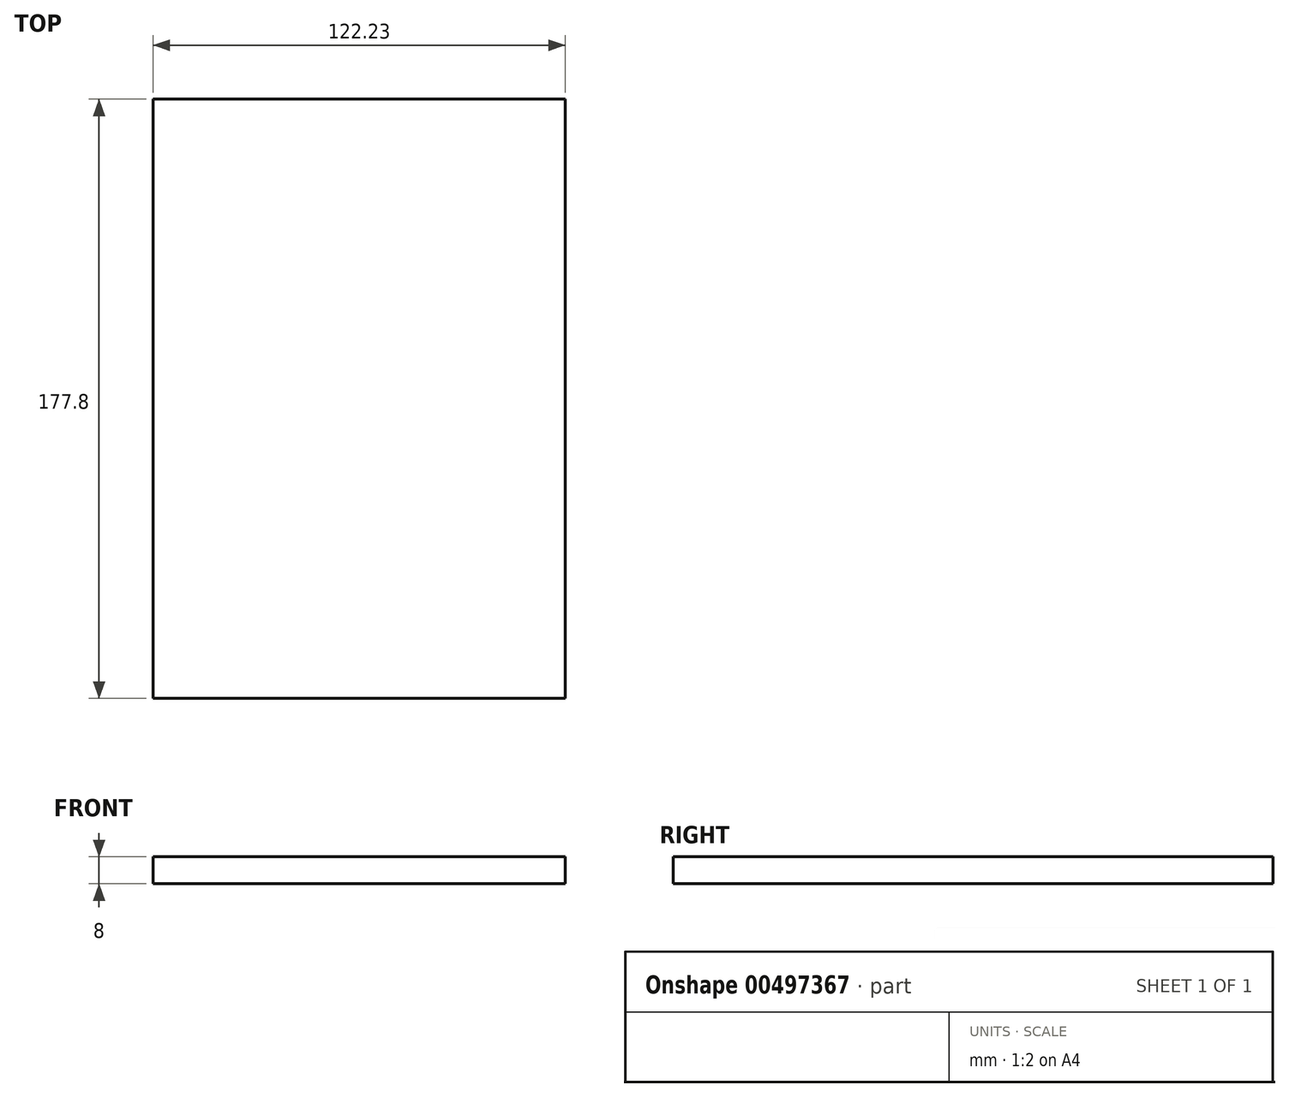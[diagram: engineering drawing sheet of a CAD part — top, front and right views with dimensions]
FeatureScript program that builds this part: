
annotation { "Feature Type Name" : "Feature", "Feature Type Description" : "" }
export const myFeature = defineFeature(function(context is Context, id is Id, definition is map)
    precondition{}
    {
        {
            var Q0;
            Q0=qCreatedBy(makeId("Front.planeOp"),FACE);
            var sketch = newSketch(context, id + "F0", { "sketchPlane" : qUnion([Q0])});
            skLineSegment(sketch, "E0.bottom", {"start": v(13.7, -4) * mm, "end": v(-108.52, -4) * mm});
            skLineSegment(sketch, "E0.top", {"start": v(13.7, 4) * mm, "end": v(-108.52, 4) * mm});
            skLineSegment(sketch, "E0.left", {"start": v(13.7, -4) * mm, "end": v(13.7, 4) * mm});
            skLineSegment(sketch, "E0.right", {"start": v(-108.52, -4) * mm, "end": v(-108.52, 4) * mm});
            skPoint(sketch, "E0.middle", {"position": v(-47.4, 0) * mm});
            skArc(sketch, "E1", {"start": v(13.7, -4) * mm, "mid": v(36.5, 5.55) * mm, "end": v(45.7, 28.48) * mm});
            skArc(sketch, "E2.0", {"start": v(13.7, 4) * mm, "mid": v(30.82, 11.18) * mm, "end": v(37.7, 28.42) * mm});
            skLineSegment(sketch, "E3", {"start": v(37.7, 28.42) * mm, "end": v(45.7, 28.48) * mm});
            skSolve(sketch);
        }
        {
            var Q0;
            Q0=makeQuery(id+"F0.imprint","IMPRINT",FACE,{"disambiguationData":[TD([[makeQuery(id+"F0.imprint","IMPRINT",EDGE,{"derivedFrom":sQuery(id+"F0.wireOp",EDGE,"E0.bottom")}),-1.0]])]});
            extrude(context, id + "F1", {"entities" : qUnion([Q0]), "endBound" : BoundingType.SYMMETRIC, "depth" : 177.8 * mm});
        }
    });
